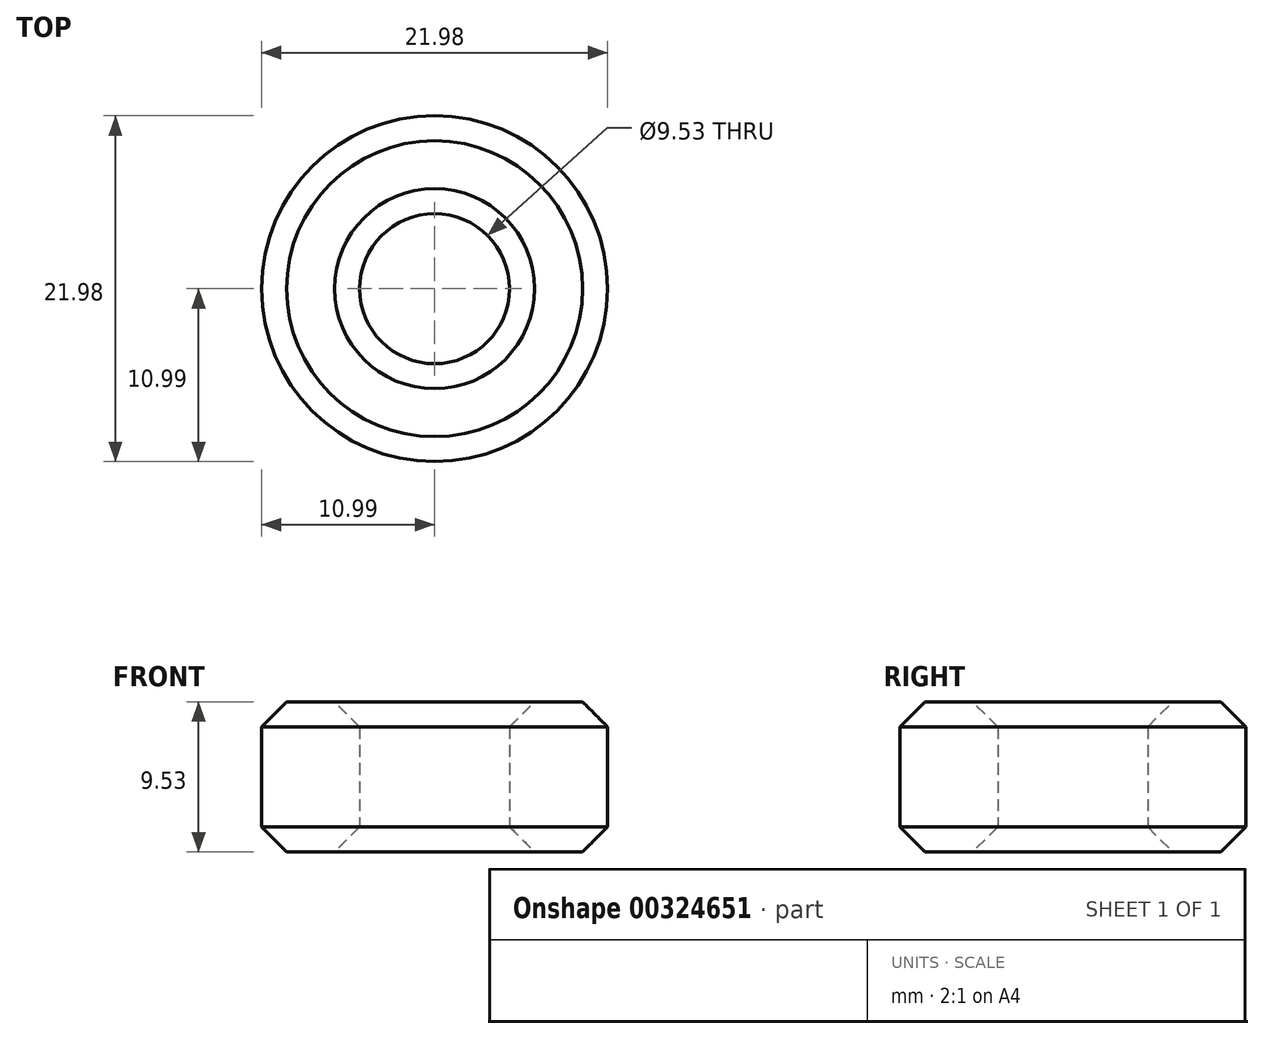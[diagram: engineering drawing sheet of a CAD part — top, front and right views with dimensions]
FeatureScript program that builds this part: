
annotation { "Feature Type Name" : "Feature", "Feature Type Description" : "" }
export const myFeature = defineFeature(function(context is Context, id is Id, definition is map)
    precondition{}
    {
        {
            var Q0;
            Q0=qCreatedBy(makeId("Top.planeOp"),FACE);
            var sketch = newSketch(context, id + "F0", { "sketchPlane" : qUnion([Q0])});
            skCircle(sketch, "E0", {"center": v(0, 0) * mm, "radius": 4.76 * mm});
            skCircle(sketch, "E1", {"center": v(0, 0) * mm, "radius": 10.99 * mm});
            skSolve(sketch);
        }
        {
            var Q0;
            Q0=makeQuery(id+"F0.imprint","IMPRINT",FACE,{"disambiguationData":[TD([[makeQuery(id+"F0.imprint","IMPRINT",EDGE,{"derivedFrom":sQuery(id+"F0.wireOp",EDGE,"E0")}),-1.0]])]});
            extrude(context, id + "F1", {"entities" : qUnion([Q0]), "depth" : 9.52 * mm});
        }
        {
            var Q0;
            Q0=makeQuery(id+"F1.opExtrude","CAP_EDGE",EDGE,{"disambiguationData":[OSD([sQuery(id+"F0.wireOp",EDGE,"E1")])],"isStart":true});
            var Q1;
            Q1=makeQuery(id+"F1.opExtrude","CAP_EDGE",EDGE,{"disambiguationData":[OSD([sQuery(id+"F0.wireOp",EDGE,"E1")])],"isStart":false});
            var Q2;
            Q2=makeQuery(id+"F1.opExtrude","CAP_EDGE",EDGE,{"disambiguationData":[OSD([sQuery(id+"F0.wireOp",EDGE,"E0")])],"isStart":false});
            var Q3;
            Q3=makeQuery(id+"F1.opExtrude","CAP_EDGE",EDGE,{"disambiguationData":[OSD([sQuery(id+"F0.wireOp",EDGE,"E0")])],"isStart":true});
            chamfer(context, id + "F2", {"entities" : qUnion([Q0, Q1, Q2, Q3]), "width" : 1.59 * mm, "tangentPropagation" : true});
        }
    });
